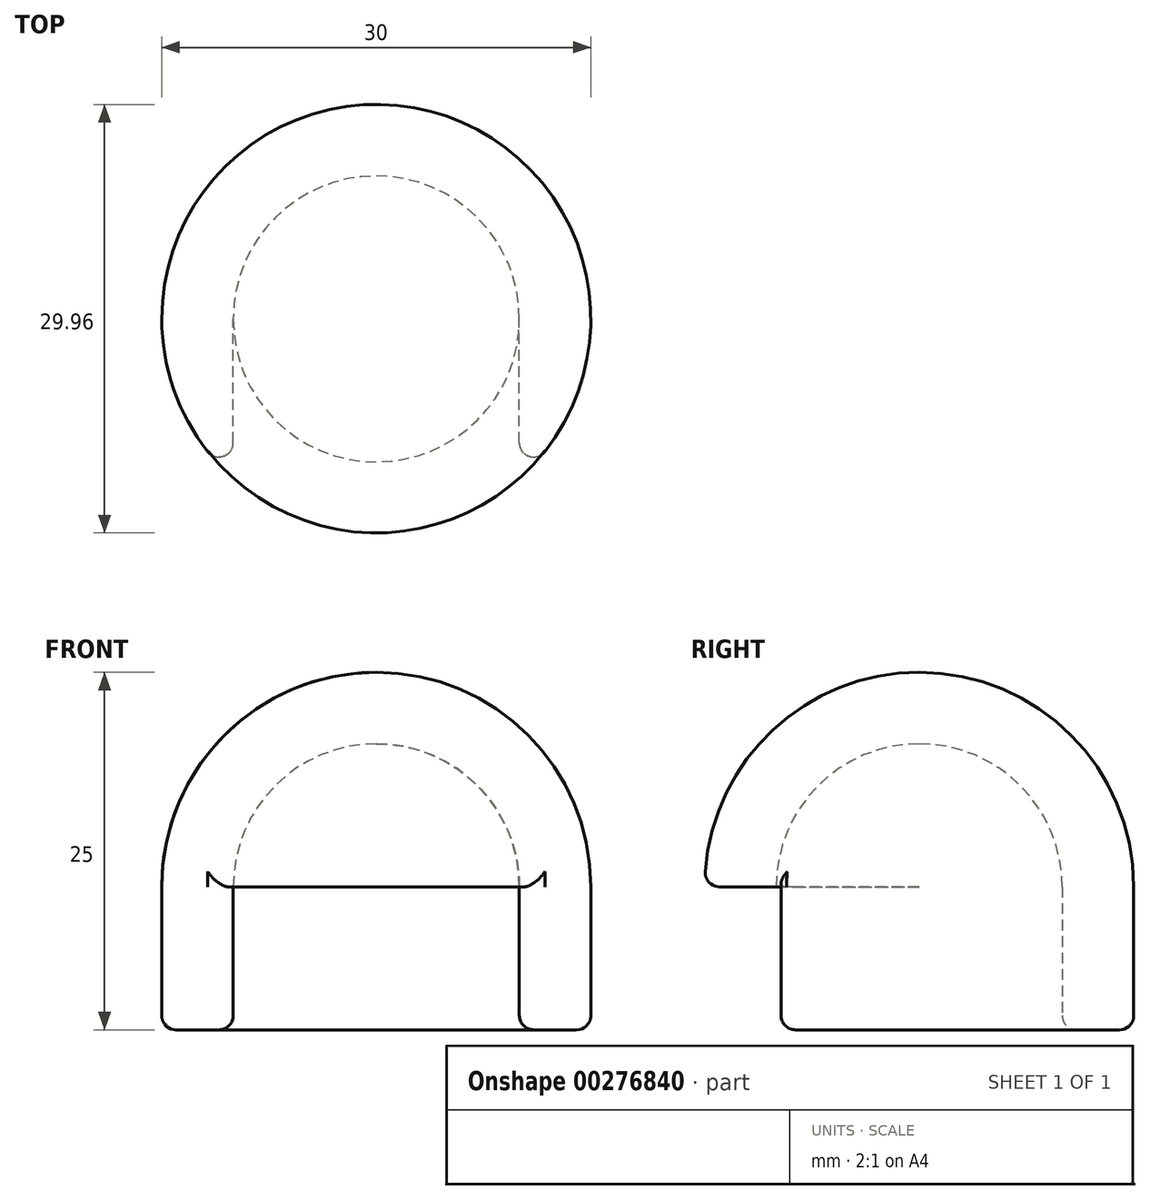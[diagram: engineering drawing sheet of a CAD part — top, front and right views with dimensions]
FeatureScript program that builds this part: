
annotation { "Feature Type Name" : "Feature", "Feature Type Description" : "" }
export const myFeature = defineFeature(function(context is Context, id is Id, definition is map)
    precondition{}
    {
        {
            var Q0;
            Q0=qCreatedBy(makeId("Front.planeOp"),FACE);
            var sketch = newSketch(context, id + "F0", { "sketchPlane" : qUnion([Q0])});
            skCircle(sketch, "E0", {"center": v(0, 0) * mm, "radius": 10 * mm});
            skCircle(sketch, "E1", {"center": v(0, 0) * mm, "radius": 15 * mm});
            skLineSegment(sketch, "E2", {"start": v(-15, 0) * mm, "end": v(15, 0) * mm});
            skLineSegment(sketch, "E3", {"start": v(-15, 0) * mm, "end": v(-15, -10) * mm});
            skLineSegment(sketch, "E4", {"start": v(-15, -10) * mm, "end": v(15, -10) * mm});
            skLineSegment(sketch, "E5", {"start": v(15, -10) * mm, "end": v(15, 0) * mm});
            skLineSegment(sketch, "E6", {"start": v(0, -10) * mm, "end": v(0, 15) * mm});
            skPoint(sketch, "E7", {"position": v(-10, 0) * mm});
            skPoint(sketch, "E8", {"position": v(10, 0) * mm});
            skLineSegment(sketch, "E9", {"start": v(-10, 0) * mm, "end": v(-10, -10) * mm});
            skLineSegment(sketch, "E10", {"start": v(10, 0) * mm, "end": v(10, -10) * mm});
            skSolve(sketch);
        }
        {
            var Q0;
            {var subQ3=sQuery(id+"F0.wireOp",EDGE,"E6");var subQ5=sQuery(id+"F0.wireOp",EDGE,"E1");var subQ6=makeQuery(id+"F0.imprint","INTERSECT",VERTEX,{"derivedFrom":[subQ5,subQ3]});Q0=makeQuery(id+"F0.imprint","IMPRINT",FACE,{"disambiguationData":[TD([[makeQuery(id+"F0.imprint","IMPRINT",EDGE,{"disambiguationData":[TD([[subQ6,1.0]])],"derivedFrom":subQ3}),1.0]])]});}
            var Q1;
            {var subQ5=sQuery(id+"F0.wireOp",EDGE,"E9");Q1=makeQuery(id+"F0.imprint","IMPRINT",FACE,{"disambiguationData":[TD([[makeQuery(id+"F0.imprint","IMPRINT",EDGE,{"derivedFrom":subQ5}),-1.0]])]});}
            var Q2;
            {var subQ0=sQuery(id+"F0.wireOp",EDGE,"E3");Q2=makeQuery(id+"F0.imprint","IMPRINT",FACE,{"disambiguationData":[TD([[makeQuery(id+"F0.imprint","IMPRINT",EDGE,{"derivedFrom":subQ0}),1.0]])]});}
            var Q3;
            Q3=sQuery(id+"F0.wireOp",EDGE,"E6");
            revolve(context, id + "F1", {"entities" : qUnion([Q0, Q1, Q2]), "axis" : qUnion([Q3]), "revolveType" : RevolveType.FULL});
        }
        {
            var Q0;
            {var subQ3=sQuery(id+"F0.wireOp",EDGE,"E10");Q0=makeQuery(id+"F0.imprint","IMPRINT",FACE,{"disambiguationData":[TD([[makeQuery(id+"F0.imprint","IMPRINT",EDGE,{"derivedFrom":subQ3}),-1.0]])]});}
            var Q1;
            {var subQ0=sQuery(id+"F0.wireOp",EDGE,"E6");var subQ3=sQuery(id+"F0.wireOp",EDGE,"E2");var subQ5=makeQuery(id+"F0.imprint","INTERSECT",VERTEX,{"derivedFrom":[subQ3,subQ0]});Q1=makeQuery(id+"F0.imprint","IMPRINT",FACE,{"disambiguationData":[TD([[makeQuery(id+"F0.imprint","IMPRINT",EDGE,{"disambiguationData":[TD([[subQ5,-1.0]])],"derivedFrom":subQ3}),-1.0]])]});}
            var Q2;
            {var subQ0=sQuery(id+"F0.wireOp",EDGE,"E6");var subQ3=sQuery(id+"F0.wireOp",EDGE,"E2");var subQ5=makeQuery(id+"F0.imprint","INTERSECT",VERTEX,{"derivedFrom":[subQ3,subQ0]});Q2=makeQuery(id+"F0.imprint","IMPRINT",FACE,{"disambiguationData":[TD([[makeQuery(id+"F0.imprint","IMPRINT",EDGE,{"disambiguationData":[TD([[subQ5,1.0]])],"derivedFrom":subQ3}),-1.0]])]});}
            var Q3;
            {var subQ3=sQuery(id+"F0.wireOp",EDGE,"E9");Q3=makeQuery(id+"F0.imprint","IMPRINT",FACE,{"disambiguationData":[TD([[makeQuery(id+"F0.imprint","IMPRINT",EDGE,{"derivedFrom":subQ3}),1.0]])]});}
            extrude(context, id + "F2", {"entities" : qUnion([Q0, Q1, Q2, Q3]), "operationType" : NewBodyOperationType.REMOVE, "depth" : 25 * mm});
        }
        {
            var Q0;
            Q0=makeQuery(id+"F1.opRevolve","SWEPT_EDGE",EDGE,{"disambiguationData":[OSD([sQuery(id+"F0.wireOp",EDGE,"E3"),sQuery(id+"F0.wireOp",EDGE,"E4")])]});
            var Q1;
            Q1=makeQuery(id+"F2.boolean.opBoolean","INTERSECT",EDGE,{"derivedFrom":[makeQuery(id+"F1.opRevolve","SWEPT_FACE",FACE,{"disambiguationData":[OSD([sQuery(id+"F0.wireOp",EDGE,"E3")])]}),makeQuery(id+"F2.opExtrude","SWEPT_FACE",FACE,{"disambiguationData":[OSD([sQuery(id+"F0.wireOp",EDGE,"E9")])]})]});
            var Q2;
            Q2=makeQuery(id+"F2.boolean.opBoolean","SPLIT",EDGE,{"disambiguationData":[OD(0.0)],"derivedFrom":makeQuery(id+"F1.opRevolve","SWEPT_EDGE",EDGE,{"disambiguationData":[OSD([sQuery(id+"F0.wireOp",EDGE,"E1"),sQuery(id+"F0.wireOp",EDGE,"E2"),sQuery(id+"F0.wireOp",EDGE,"E3")])]})});
            var Q3;
            Q3=makeQuery(id+"F2.boolean.opBoolean","INTERSECT",EDGE,{"derivedFrom":[makeQuery(id+"F1.opRevolve","SWEPT_FACE",FACE,{"disambiguationData":[OSD([sQuery(id+"F0.wireOp",EDGE,"E3")])]}),makeQuery(id+"F2.opExtrude","SWEPT_FACE",FACE,{"disambiguationData":[OSD([sQuery(id+"F0.wireOp",EDGE,"E10")])]})]});
            var Q4;
            Q4=makeQuery(id+"F1.opRevolve","SWEPT_EDGE",EDGE,{"disambiguationData":[OSD([sQuery(id+"F0.wireOp",EDGE,"E4"),sQuery(id+"F0.wireOp",EDGE,"E9")])]});
            fillet(context, id + "F3", {"entities" : qUnion([Q0, Q1, Q2, Q3, Q4]), "radius" : 1 * mm, "tangentPropagation" : true, "allowEdgeOverflow" : false});
        }
    });
